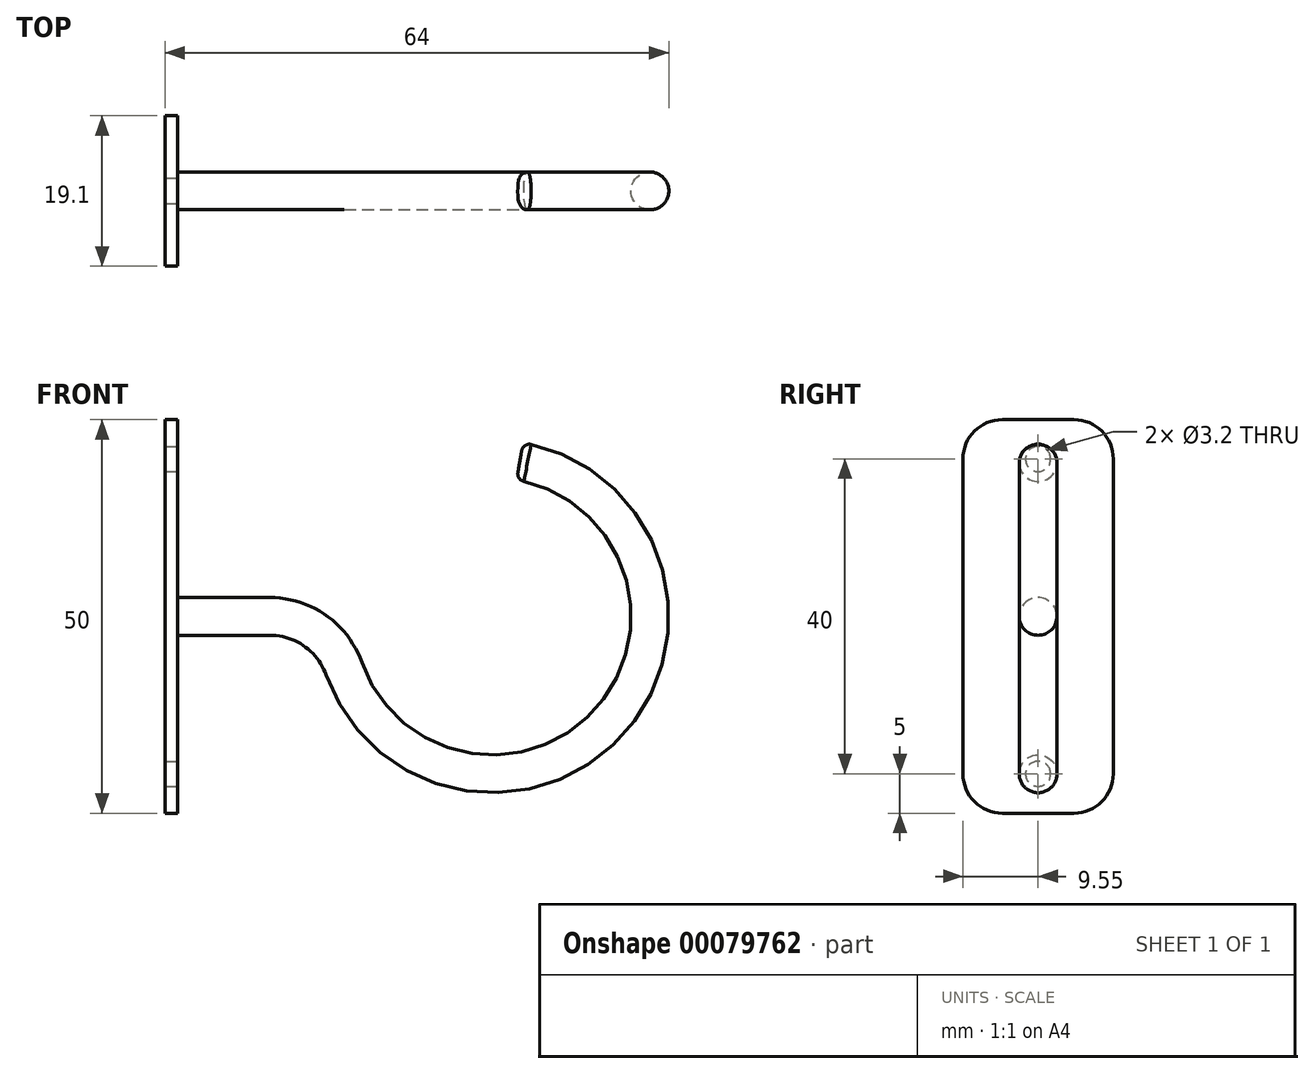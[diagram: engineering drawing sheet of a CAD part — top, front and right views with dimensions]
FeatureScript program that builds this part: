
annotation { "Feature Type Name" : "Feature", "Feature Type Description" : "" }
export const myFeature = defineFeature(function(context is Context, id is Id, definition is map)
    precondition{}
    {
        {
            var Q0;
            Q0=qCreatedBy(makeId("Front.planeOp"),FACE);
            var sketch = newSketch(context, id + "F0", { "sketchPlane" : qUnion([Q0])});
            skLineSegment(sketch, "E0", {"start": v(0, 0) * mm, "end": v(11.72, 0) * mm});
            skArc(sketch, "E1", {"start": v(21.14, -6.67) * mm, "mid": v(55.26, -12.93) * mm, "end": v(43.47, 19.7) * mm});
            skLineSegment(sketch, "E2", {"start": v(20, 0) * mm, "end": v(40, 0) * mm, "construction": true});
            skLineSegment(sketch, "E3", {"start": v(43.47, 19.7) * mm, "end": v(40, 0) * mm, "construction": true});
            skPoint(sketch, "E4.visualSharp", {"position": v(20, 0) * mm});
            skArc(sketch, "E4.filletArc", {"start": v(21.14, -6.67) * mm, "mid": v(17.49, -1.84) * mm, "end": v(11.72, 0) * mm});
            skSolve(sketch);
        }
        {
            var Q0;
            Q0=qCreatedBy(makeId("Right.planeOp"),FACE);
            var sketch = newSketch(context, id + "F1", { "sketchPlane" : qUnion([Q0])});
            skCircle(sketch, "E5", {"center": v(0, 0) * mm, "radius": 2.4 * mm});
            skSolve(sketch);
        }
        {
            var Q0;
            Q0=makeQuery(id+"F1.imprint","IMPRINT",FACE,{"disambiguationData":[TD([[makeQuery(id+"F1.imprint","IMPRINT",EDGE,{"derivedFrom":sQuery(id+"F1.wireOp",EDGE,"E5")}),1.0]])]});
            var Q1;
            Q1=sQuery(id+"F0.wireOp",EDGE,"E4.filletArc");
            var Q2;
            Q2=sQuery(id+"F0.wireOp",EDGE,"E1");
            var Q3;
            Q3=sQuery(id+"F0.wireOp",EDGE,"E0");
            sweep(context, id + "F2", {"profiles" : qUnion([Q0]), "path" : qUnion([Q1, Q2, Q3])});
        }
        {
            var Q0;
            Q0=qCreatedBy(makeId("Right.planeOp"),FACE);
            var sketch = newSketch(context, id + "F3", { "sketchPlane" : qUnion([Q0])});
            skLineSegment(sketch, "E6.bottom", {"start": v(-9.55, -25) * mm, "end": v(9.55, -25) * mm});
            skLineSegment(sketch, "E6.top", {"start": v(-9.55, 25) * mm, "end": v(9.55, 25) * mm});
            skLineSegment(sketch, "E6.left", {"start": v(-9.55, -25) * mm, "end": v(-9.55, 25) * mm});
            skLineSegment(sketch, "E6.right", {"start": v(9.55, -25) * mm, "end": v(9.55, 25) * mm});
            skPoint(sketch, "E6.middle", {"position": v(0, 0) * mm});
            skCircle(sketch, "E7", {"center": v(0, 20) * mm, "radius": 1.6 * mm});
            skCircle(sketch, "E8", {"center": v(0, -20) * mm, "radius": 1.6 * mm});
            skSolve(sketch);
        }
        {
            var Q0;
            Q0=qSketchRegion(id+"F3",true);
            extrude(context, id + "F4", {"entities" : qUnion([Q0]), "operationType" : NewBodyOperationType.ADD, "oppositeDirection" : true, "depth" : 1.6 * mm});
        }
        {
            var Q0;
            Q0=makeQuery(id+"F4.opExtrude","SWEPT_EDGE",EDGE,{"disambiguationData":[OSD([sQuery(id+"F3.wireOp",EDGE,"E6.top"),sQuery(id+"F3.wireOp",EDGE,"E6.left")])]});
            var Q1;
            Q1=makeQuery(id+"F4.opExtrude","SWEPT_EDGE",EDGE,{"disambiguationData":[OSD([sQuery(id+"F3.wireOp",EDGE,"E6.top"),sQuery(id+"F3.wireOp",EDGE,"E6.right")])]});
            var Q2;
            Q2=makeQuery(id+"F4.opExtrude","SWEPT_EDGE",EDGE,{"disambiguationData":[OSD([sQuery(id+"F3.wireOp",EDGE,"E6.bottom"),sQuery(id+"F3.wireOp",EDGE,"E6.left")])]});
            var Q3;
            Q3=makeQuery(id+"F4.opExtrude","SWEPT_EDGE",EDGE,{"disambiguationData":[OSD([sQuery(id+"F3.wireOp",EDGE,"E6.bottom"),sQuery(id+"F3.wireOp",EDGE,"E6.right")])]});
            fillet(context, id + "F5", {"entities" : qUnion([Q0, Q1, Q2, Q3]), "radius" : 5 * mm, "tangentPropagation" : true, "allowEdgeOverflow" : false});
        }
        {
            var Q0;
            Q0=makeQuery(id+"F2.opSweep","CAP_EDGE",EDGE,{"disambiguationData":[OSD([sQuery(id+"F0.wireOp",VERTEX,"E1.end"),sQuery(id+"F1.wireOp",EDGE,"E5")])],"isStart":false});
            fillet(context, id + "F6", {"entities" : qUnion([Q0]), "radius" : 1 * mm, "tangentPropagation" : true, "allowEdgeOverflow" : false});
        }
    });
